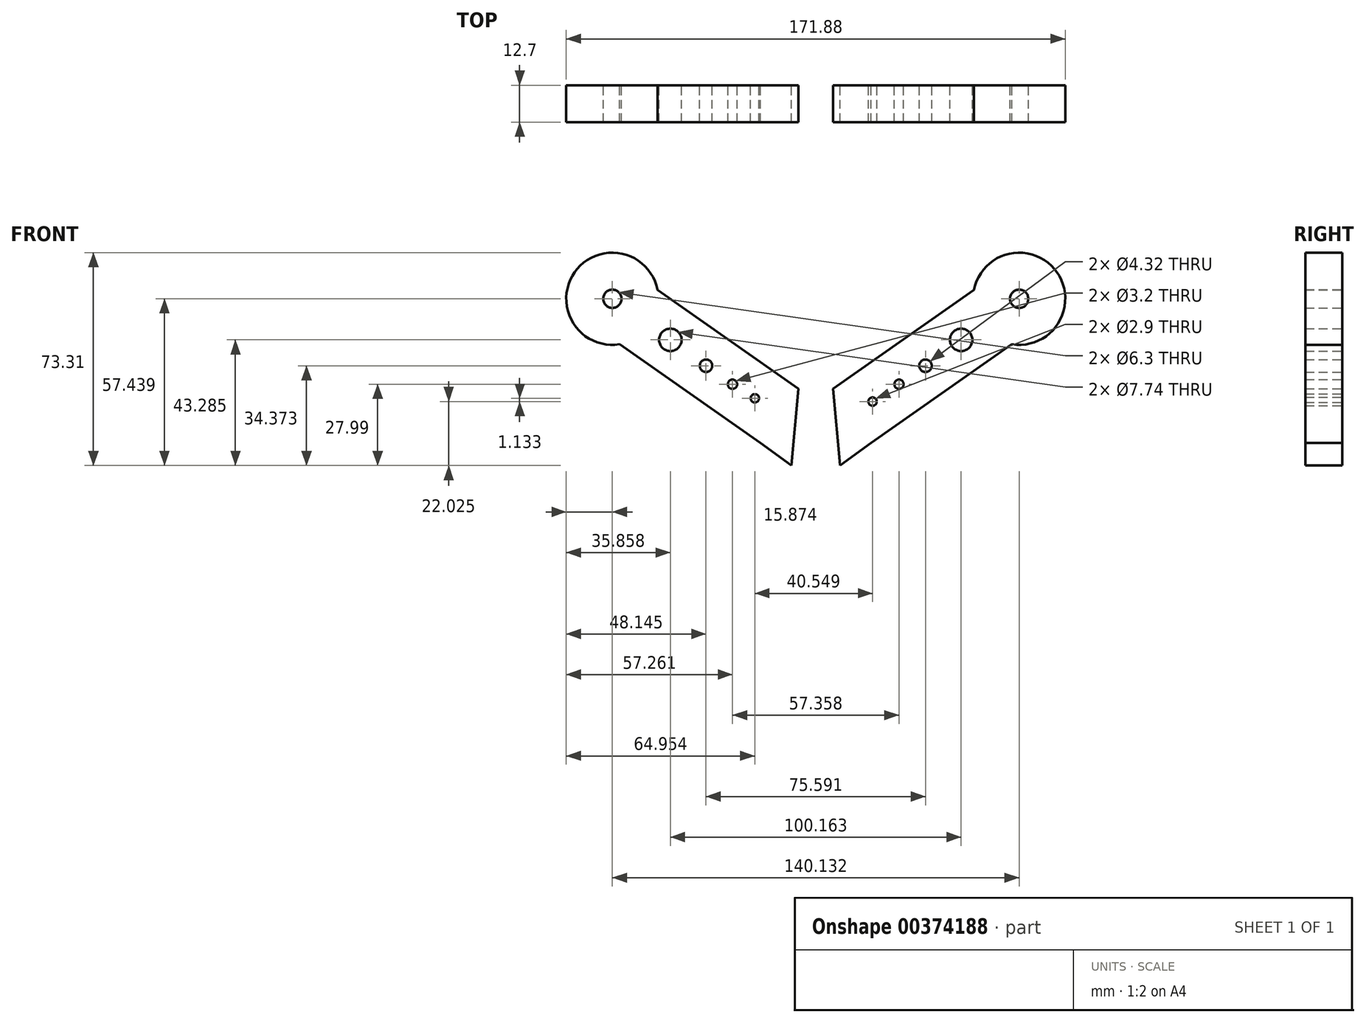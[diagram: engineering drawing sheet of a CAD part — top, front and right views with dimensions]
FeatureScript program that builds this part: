
annotation { "Feature Type Name" : "Feature", "Feature Type Description" : "" }
export const myFeature = defineFeature(function(context is Context, id is Id, definition is map)
    precondition{}
    {
        {
            var Q0;
            Q0=qCreatedBy(makeId("Front.planeOp"),FACE);
            var sketch = newSketch(context, id + "F0", { "sketchPlane" : qUnion([Q0])});
            skLineSegment(sketch, "E0.bottom", {"start": v(-5.96, 13.84) * mm, "end": v(-54.48, 47.8) * mm});
            skLineSegment(sketch, "E0.top", {"start": v(-19.07, -4.9) * mm, "end": v(-67.6, 29.08) * mm});
            skLineSegment(sketch, "E0.left", {"start": v(-5.96, 13.84) * mm, "end": v(-19.07, -4.9) * mm});
            skLineSegment(sketch, "E0.right", {"start": v(-54.48, 47.8) * mm, "end": v(-67.6, 29.08) * mm});
            skCircle(sketch, "E1", {"center": v(-70.07, 44.77) * mm, "radius": 15.88 * mm});
            skPoint(sketch, "E1.centerSnap0", {"position": v(-61.04, 38.45) * mm});
            skLineSegment(sketch, "E2", {"start": v(0, 76.66) * mm, "end": v(0, -76.54) * mm});
            skCircle(sketch, "E3", {"center": v(-50.08, 30.62) * mm, "radius": 3.87 * mm});
            skCircle(sketch, "E4", {"center": v(-37.8, 21.7) * mm, "radius": 2.16 * mm});
            skCircle(sketch, "E5", {"center": v(-28.68, 15.32) * mm, "radius": 1.6 * mm});
            skCircle(sketch, "E6", {"center": v(-70.07, 44.77) * mm, "radius": 3.15 * mm});
            skLineSegment(sketch, "E7", {"start": v(-8.33, -12.67) * mm, "end": v(-19.07, -4.9) * mm});
            skLineSegment(sketch, "E8", {"start": v(-8.33, -12.67) * mm, "end": v(-5.96, 13.84) * mm});
            skCircle(sketch, "E9.MirrorC", {"center": v(28.68, 15.32) * mm, "radius": 1.6 * mm});
            skLineSegment(sketch, "E10.MirrorCS", {"start": v(8.33, -12.67) * mm, "end": v(5.96, 13.84) * mm});
            skLineSegment(sketch, "E11.MirrorCS", {"start": v(8.33, -12.67) * mm, "end": v(19.07, -4.9) * mm});
            skCircle(sketch, "E12.MirrorC", {"center": v(70.07, 44.77) * mm, "radius": 3.15 * mm});
            skCircle(sketch, "E13.MirrorC", {"center": v(37.8, 21.7) * mm, "radius": 2.16 * mm});
            skCircle(sketch, "E14.MirrorC", {"center": v(50.08, 30.62) * mm, "radius": 3.87 * mm});
            skCircle(sketch, "E15.MirrorC", {"center": v(70.07, 44.77) * mm, "radius": 15.88 * mm});
            skLineSegment(sketch, "E16.MirrorCS", {"start": v(54.48, 47.8) * mm, "end": v(67.6, 29.08) * mm});
            skLineSegment(sketch, "E17.MirrorCS", {"start": v(5.96, 13.84) * mm, "end": v(19.07, -4.9) * mm});
            skLineSegment(sketch, "E18.MirrorCS", {"start": v(19.07, -4.9) * mm, "end": v(67.6, 29.08) * mm});
            skPoint(sketch, "E19.MirrorP", {"position": v(61.04, 38.45) * mm});
            skLineSegment(sketch, "E20.MirrorCS", {"start": v(5.96, 13.84) * mm, "end": v(54.48, 47.8) * mm});
            skCircle(sketch, "E21", {"center": v(-20.99, 10.49) * mm, "radius": 1.45 * mm});
            skCircle(sketch, "E22", {"center": v(19.56, 9.35) * mm, "radius": 1.45 * mm});
            skSolve(sketch);
        }
        {
            var Q0;
            Q0=qSketchRegion(id+"F0",true);
            extrude(context, id + "F1", {"entities" : qUnion([Q0]), "endBound" : BoundingType.SYMMETRIC, "depth" : 12.7 * mm});
        }
    });
